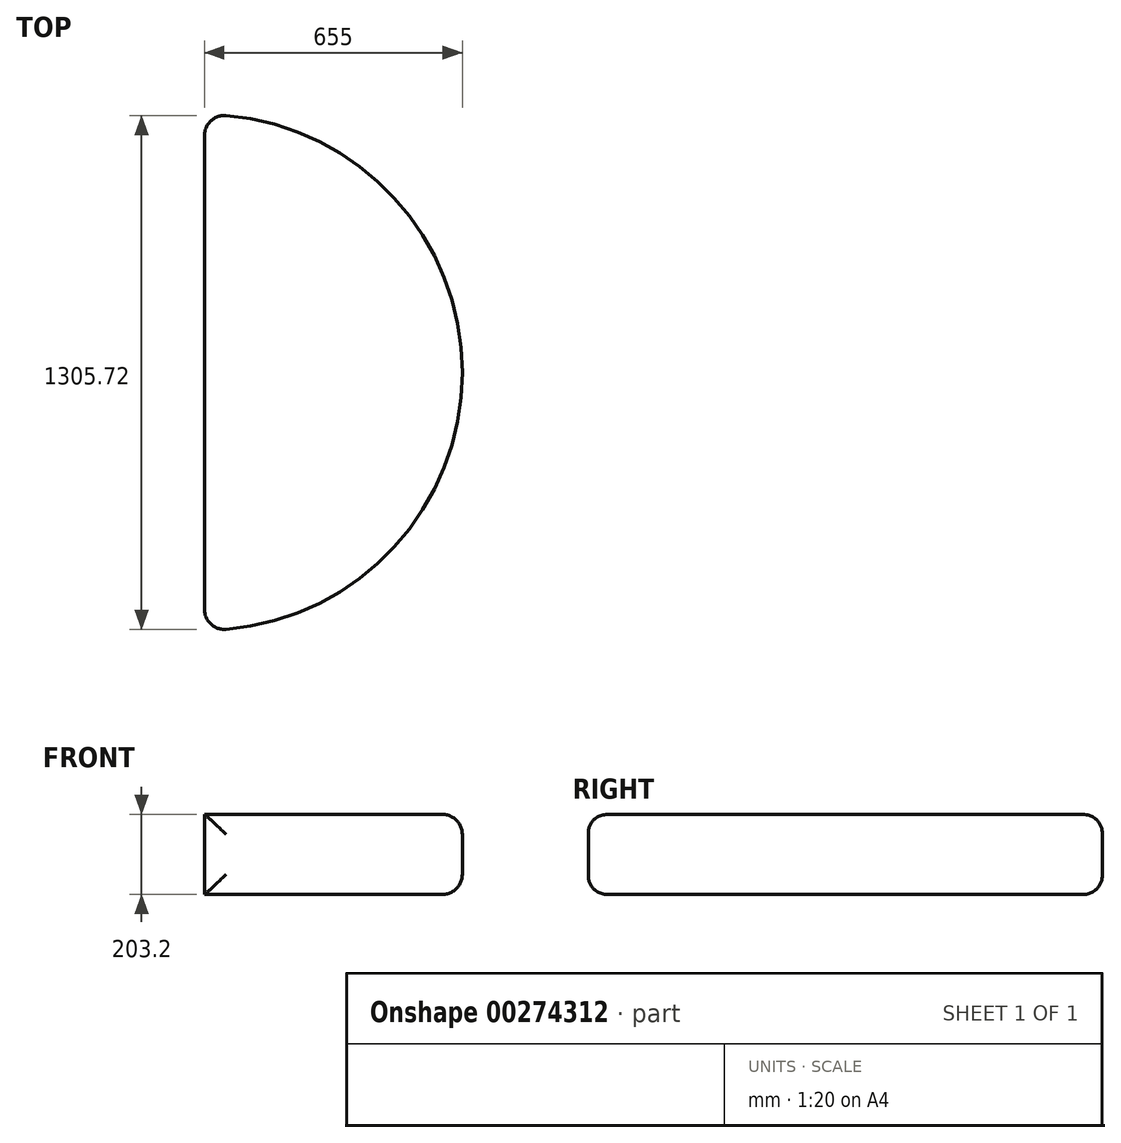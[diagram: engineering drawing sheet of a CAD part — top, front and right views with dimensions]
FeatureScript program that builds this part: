
annotation { "Feature Type Name" : "Feature", "Feature Type Description" : "" }
export const myFeature = defineFeature(function(context is Context, id is Id, definition is map)
    precondition{}
    {
        {
            var Q0;
            Q0=qCreatedBy(makeId("Top.planeOp"),FACE);
            var sketch = newSketch(context, id + "F0", { "sketchPlane" : qUnion([Q0])});
            skLineSegment(sketch, "E0", {"start": v(0, 655) * mm, "end": v(0, -655) * mm});
            skArc(sketch, "E1", {"start": v(0, 655) * mm, "mid": v(655, 0) * mm, "end": v(0, -655) * mm});
            skSolve(sketch);
        }
        {
            var Q0;
            Q0 = qSketchRegion(id + "F0", true);
            extrude(context, id + "F1", {"entities" : qUnion([Q0]), "depth" : 203.2 * mm});
        }
        {
            var Q0;
            Q0=makeQuery(id+"F1.opExtrude","CAP_EDGE",EDGE,{"disambiguationData":[OSD([sQuery(id+"F0.wireOp",EDGE,"E1")])],"isStart":false});
            var Q1;
            Q1=makeQuery(id+"F1.opExtrude","CAP_EDGE",EDGE,{"disambiguationData":[OSD([sQuery(id+"F0.wireOp",EDGE,"E1")])],"isStart":true});
            var Q2;
            {var subQ0=sQuery(id+"F0.wireOp",EDGE,"E1");var subQ1=sQuery(id+"F0.wireOp",EDGE,"E0");Q2=makeQuery(id+"F1.opExtrude","SWEPT_EDGE",EDGE,{"disambiguationData":[OSD([subQ1,subQ0]),TDD([makeQuery(id+"F0.imprint","INTERSECT",VERTEX,{"disambiguationData":[OD(1.0)],"derivedFrom":[subQ1,subQ0]})])]});}
            var Q3;
            {var subQ0=sQuery(id+"F0.wireOp",EDGE,"E1");var subQ1=sQuery(id+"F0.wireOp",EDGE,"E0");Q3=makeQuery(id+"F1.opExtrude","SWEPT_EDGE",EDGE,{"disambiguationData":[OSD([subQ1,subQ0]),TDD([makeQuery(id+"F0.imprint","INTERSECT",VERTEX,{"disambiguationData":[OD(0.0)],"derivedFrom":[subQ1,subQ0]})])]});}
            fillet(context, id + "F2", {"entities" : qUnion([Q0, Q1, Q2, Q3]), "radius" : 50.8 * mm, "tangentPropagation" : true, "allowEdgeOverflow" : false});
        }
    });
